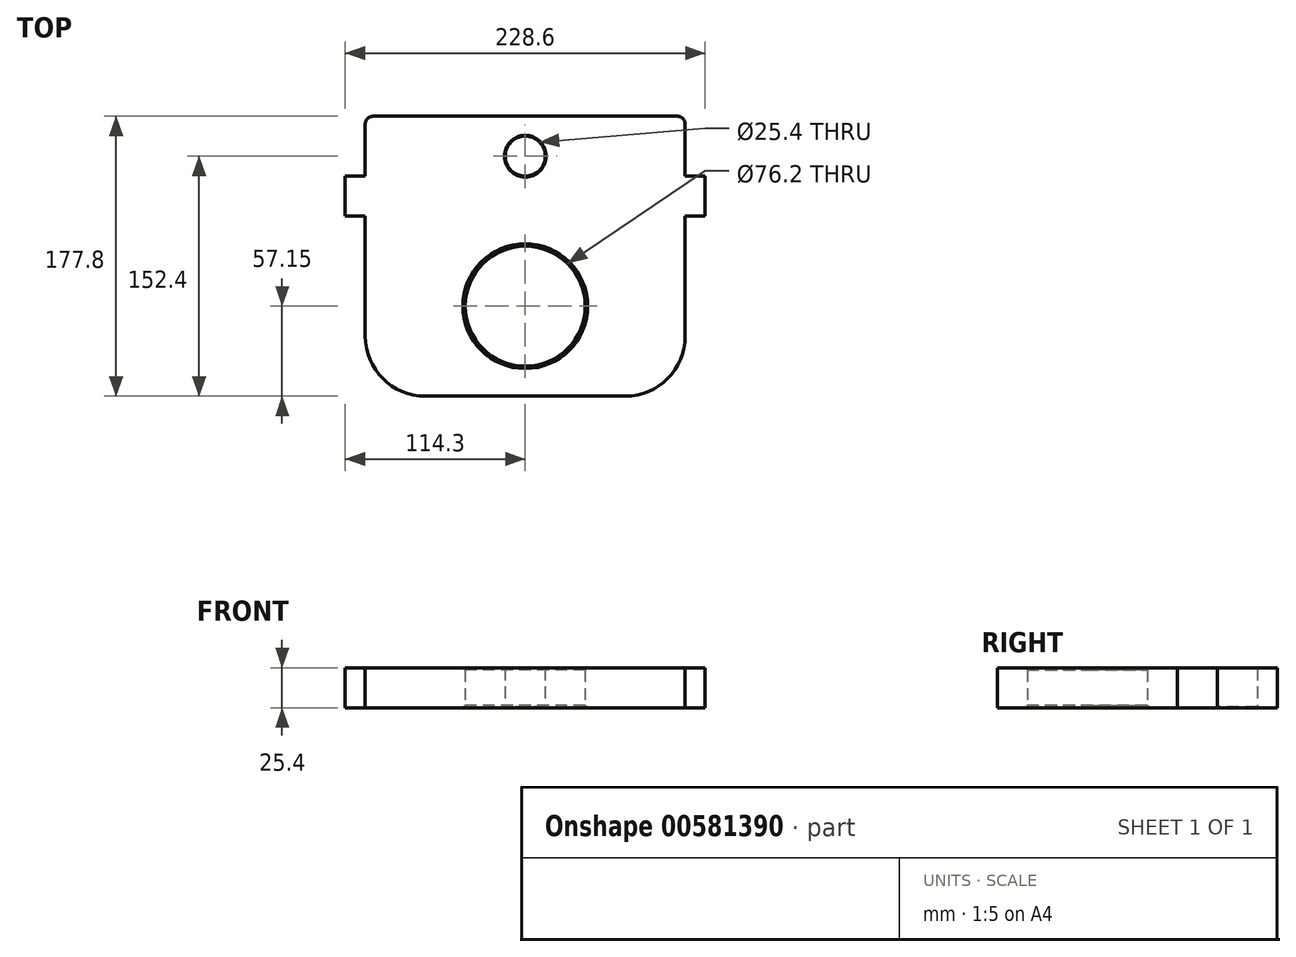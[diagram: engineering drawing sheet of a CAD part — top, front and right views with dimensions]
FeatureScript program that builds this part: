
annotation { "Feature Type Name" : "Feature", "Feature Type Description" : "" }
export const myFeature = defineFeature(function(context is Context, id is Id, definition is map)
    precondition{}
    {
        {
            var Q0;
            Q0=qCreatedBy(makeId("Top.planeOp"),FACE);
            var sketch = newSketch(context, id + "F0", { "sketchPlane" : qUnion([Q0])});
            skLineSegment(sketch, "E0.bottom", {"start": v(101.6, -88.9) * mm, "end": v(-101.6, -88.9) * mm});
            skLineSegment(sketch, "E0.top", {"start": v(101.6, 88.9) * mm, "end": v(-101.6, 88.9) * mm});
            skLineSegment(sketch, "E0.left", {"start": v(101.6, -88.9) * mm, "end": v(101.6, 88.9) * mm});
            skLineSegment(sketch, "E0.right", {"start": v(-101.6, -88.9) * mm, "end": v(-101.6, 88.9) * mm});
            skPoint(sketch, "E0.middle", {"position": v(0, 0) * mm});
            skCircle(sketch, "E1", {"center": v(0, 63.5) * mm, "radius": 12.7 * mm});
            skCircle(sketch, "E2", {"center": v(0, -31.75) * mm, "radius": 38.1 * mm});
            skSolve(sketch);
        }
        {
            var Q0;
            Q0=makeQuery(id+"F0.imprint","IMPRINT",FACE,{"disambiguationData":[TD([[makeQuery(id+"F0.imprint","IMPRINT",EDGE,{"derivedFrom":sQuery(id+"F0.wireOp",EDGE,"E0.bottom")}),-1.0]])]});
            extrude(context, id + "F1", {"entities" : qUnion([Q0]), "endBound" : BoundingType.SYMMETRIC, "depth" : 25.4 * mm, "offsetDistance" : 25.4 * mm});
        }
        {
            var Q0;
            Q0=makeQuery(id+"F1.opExtrude","CAP_EDGE",EDGE,{"disambiguationData":[OSD([sQuery(id+"F0.wireOp",EDGE,"E1")])],"isStart":false});
            var Q1;
            Q1=makeQuery(id+"F1.opExtrude","CAP_EDGE",EDGE,{"disambiguationData":[OSD([sQuery(id+"F0.wireOp",EDGE,"E1")])],"isStart":true});
            chamfer(context, id + "F2", {"entities" : qUnion([Q0, Q1]), "width" : 0.5 * mm, "tangentPropagation" : true});
        }
        {
            var Q0;
            Q0=makeQuery(id+"F1.opExtrude","CAP_EDGE",EDGE,{"disambiguationData":[OSD([sQuery(id+"F0.wireOp",EDGE,"E2")])],"isStart":false});
            var Q1;
            Q1=makeQuery(id+"F1.opExtrude","CAP_EDGE",EDGE,{"disambiguationData":[OSD([sQuery(id+"F0.wireOp",EDGE,"E2")])],"isStart":true});
            chamfer(context, id + "F3", {"entities" : qUnion([Q0, Q1]), "width" : 1.52 * mm, "tangentPropagation" : true});
        }
        {
            var Q0;
            Q0=makeQuery(id+"F1.opExtrude","SWEPT_EDGE",EDGE,{"disambiguationData":[OSD([sQuery(id+"F0.wireOp",EDGE,"E0.bottom"),sQuery(id+"F0.wireOp",EDGE,"E0.right")])]});
            var Q1;
            Q1=makeQuery(id+"F1.opExtrude","SWEPT_EDGE",EDGE,{"disambiguationData":[OSD([sQuery(id+"F0.wireOp",EDGE,"E0.bottom"),sQuery(id+"F0.wireOp",EDGE,"E0.left")])]});
            fillet(context, id + "F4", {"entities" : qUnion([Q0, Q1]), "radius" : 38.1 * mm, "tangentPropagation" : true, "allowEdgeOverflow" : false});
        }
        {
            var Q0;
            Q0=makeQuery(id+"F1.opExtrude","SWEPT_EDGE",EDGE,{"disambiguationData":[OSD([sQuery(id+"F0.wireOp",EDGE,"E0.top"),sQuery(id+"F0.wireOp",EDGE,"E0.left")])]});
            var Q1;
            Q1=makeQuery(id+"F1.opExtrude","SWEPT_EDGE",EDGE,{"disambiguationData":[OSD([sQuery(id+"F0.wireOp",EDGE,"E0.top"),sQuery(id+"F0.wireOp",EDGE,"E0.right")])]});
            fillet(context, id + "F5", {"entities" : qUnion([Q0, Q1]), "radius" : 5.08 * mm, "tangentPropagation" : true, "allowEdgeOverflow" : false});
        }
        {
            var Q0;
            Q0=makeQuery(id+"F1.opExtrude","CAP_FACE",FACE,{"disambiguationData":[OSD([sQuery(id+"F0.wireOp",EDGE,"E0.bottom"),sQuery(id+"F0.wireOp",EDGE,"E0.top"),sQuery(id+"F0.wireOp",EDGE,"E0.left"),sQuery(id+"F0.wireOp",EDGE,"E0.right"),sQuery(id+"F0.wireOp",EDGE,"E1"),sQuery(id+"F0.wireOp",EDGE,"E2")])],"isStart":false});
            var sketch = newSketch(context, id + "F6", { "sketchPlane" : qUnion([Q0])});
            skLineSegment(sketch, "E3.bottom", {"start": v(114.3, 25.4) * mm, "end": v(101.6, 25.4) * mm});
            skLineSegment(sketch, "E3.top", {"start": v(114.3, 50.8) * mm, "end": v(101.6, 50.8) * mm});
            skLineSegment(sketch, "E3.left", {"start": v(114.3, 25.4) * mm, "end": v(114.3, 50.8) * mm});
            skLineSegment(sketch, "E3.right", {"start": v(-114.3, 25.4) * mm, "end": v(-114.3, 50.8) * mm});
            skPoint(sketch, "E3.middle", {"position": v(0, 38.1) * mm});
            skLineSegment(sketch, "E4", {"start": v(-101.6, 50.8) * mm, "end": v(-101.6, 25.4) * mm});
            skLineSegment(sketch, "E5", {"start": v(101.6, 50.8) * mm, "end": v(101.6, 25.4) * mm});
            skLineSegment(sketch, "E6.trimOffspring", {"start": v(-101.6, 50.8) * mm, "end": v(-114.3, 50.8) * mm});
            skLineSegment(sketch, "E7.trimOffspring", {"start": v(-101.6, 25.4) * mm, "end": v(-114.3, 25.4) * mm});
            skSolve(sketch);
        }
        {
            var Q0;
            Q0=makeQuery(id+"F6.imprint","IMPRINT",FACE,{"disambiguationData":[TD([[makeQuery(id+"F6.imprint","IMPRINT",EDGE,{"derivedFrom":sQuery(id+"F6.wireOp",EDGE,"E3.right")}),-1.0]])]});
            var Q1;
            Q1=makeQuery(id+"F6.imprint","IMPRINT",FACE,{"disambiguationData":[TD([[makeQuery(id+"F6.imprint","IMPRINT",EDGE,{"derivedFrom":sQuery(id+"F6.wireOp",EDGE,"E3.bottom")}),-1.0]])]});
            extrude(context, id + "F7", {"entities" : qUnion([Q0, Q1]), "operationType" : NewBodyOperationType.ADD, "oppositeDirection" : true, "depth" : 25.4 * mm, "offsetDistance" : 25.4 * mm});
        }
    });
